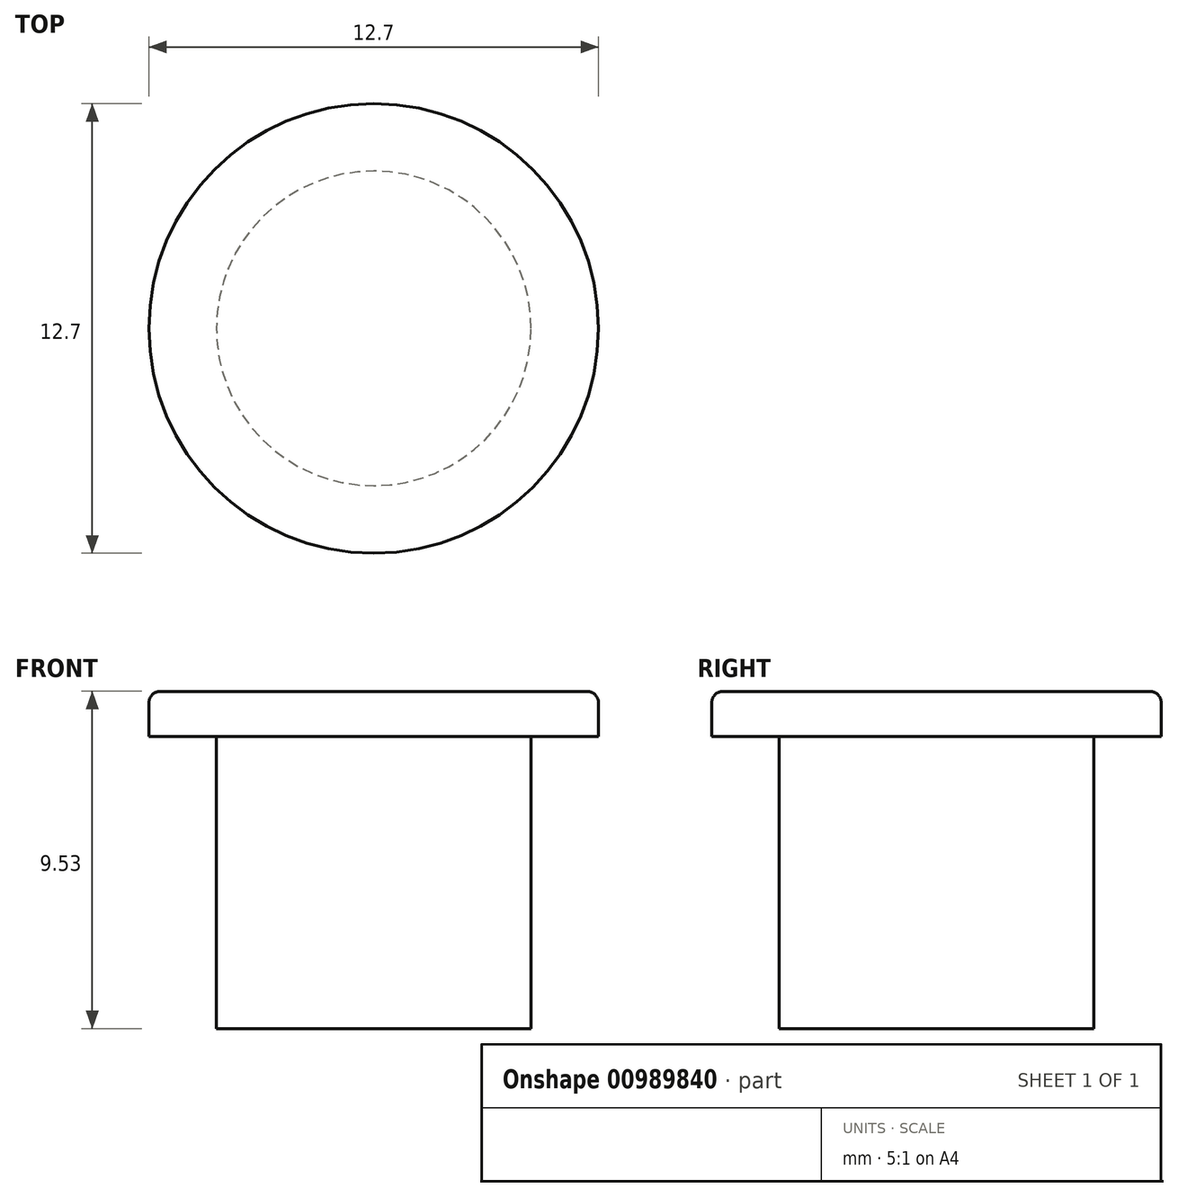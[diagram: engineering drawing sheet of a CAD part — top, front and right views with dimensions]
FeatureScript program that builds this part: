
annotation { "Feature Type Name" : "Feature", "Feature Type Description" : "" }
export const myFeature = defineFeature(function(context is Context, id is Id, definition is map)
    precondition{}
    {
        {
            var Q0;
            Q0=qCreatedBy(makeId("Top.planeOp"),FACE);
            var sketch = newSketch(context, id + "F0", { "sketchPlane" : qUnion([Q0])});
            skCircle(sketch, "E0", {"center": v(0, 0) * mm, "radius": 4.45 * mm});
            skSolve(sketch);
        }
        {
            var Q0;
            Q0=makeQuery(id+"F0.imprint","IMPRINT",FACE,{"disambiguationData":[TD([[makeQuery(id+"F0.imprint","IMPRINT",EDGE,{"derivedFrom":sQuery(id+"F0.wireOp",EDGE,"E0")}),1.0]])]});
            extrude(context, id + "F1", {"entities" : qUnion([Q0]), "depth" : 9.52 * mm, "offsetDistance" : 25.4 * mm});
        }
        {
            var Q0;
            Q0=makeQuery(id+"F1.opExtrude","CAP_FACE",FACE,{"disambiguationData":[OSD([sQuery(id+"F0.wireOp",EDGE,"E0")])],"isStart":false});
            var sketch = newSketch(context, id + "F2", { "sketchPlane" : qUnion([Q0])});
            skCircle(sketch, "E1.0.0", {"center": v(0, 0) * mm, "radius": 4.45 * mm});
            skCircle(sketch, "E2", {"center": v(0, 0) * mm, "radius": 6.35 * mm});
            skSolve(sketch);
        }
        {
            var Q0;
            Q0=makeQuery(id+"F2.imprint","IMPRINT",FACE,{"disambiguationData":[TD([[makeQuery(id+"F2.imprint","IMPRINT",EDGE,{"derivedFrom":sQuery(id+"F2.wireOp",EDGE,"E1.0.0")}),-1.0]])]});
            extrude(context, id + "F3", {"entities" : qUnion([Q0]), "operationType" : NewBodyOperationType.ADD, "oppositeDirection" : true, "depth" : 1.27 * mm, "offsetDistance" : 25.4 * mm});
        }
        {
            var Q0;
            Q0=makeQuery(id+"F3.boolean.opBoolean","MERGE",FACE,{"derivedFrom":[makeQuery(id+"F1.opExtrude","CAP_FACE",FACE,{"disambiguationData":[OSD([sQuery(id+"F0.wireOp",EDGE,"E0")])],"isStart":false}),makeQuery(id+"F3.opExtrude","CAP_FACE",FACE,{"disambiguationData":[OSD([sQuery(id+"F2.wireOp",EDGE,"E1.0.0"),sQuery(id+"F2.wireOp",EDGE,"E2")])],"isStart":true})]});
            fillet(context, id + "F4", {"entities" : qUnion([Q0]), "radius" : 0.32 * mm, "tangentPropagation" : true, "allowEdgeOverflow" : false});
        }
    });
